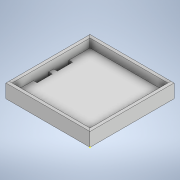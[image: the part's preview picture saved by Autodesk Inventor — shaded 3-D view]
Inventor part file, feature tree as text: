
AUTODESK INVENTOR PART (.ipt)
format: ipt  version: 2021 (Build 250183000, 183)  size: 198,656 bytes
history: native  units: in
note: dims shown in document units (in); Inventor stores cm internally (conversion verified against a paired STEP export)
features: sketch x5, extrude x4, projected_geometry x3, chamfer x2
ambient origin geometry x8: Origin, YZ Plane, XZ Plane, XY Plane, X Axis, Y Axis, Z Axis, Center Point
bodies: Solid1 (feature_tree)
feature tree (14):
  sketch  "Sketch1"  dims[d0=1.3071in d1=1.3071in]
  extrude  "Extrusion1"  Depth=1.3071in
  extrude  "Extrusion2"  Depth=0.0472in
  chamfer  "Chamfer1"  Distance=0.1575in
  extrude  "Extrusion3"  Depth=0.0787in TaperAngle=45.0deg
  extrude  "Extrusion4"  Depth=0.0394in
  chamfer  "Chamfer2"  Distance=0.0591in
  sketch  "Sketch2"  dims[d2=0.0787in d3=0.0in d4=0.0472in]
  sketch  "Sketch3"  dims[d5=0.0472in]
  projected_geometry  "Projected Loop1"
  sketch  "Sketch4"  dims[d6=1.2126in]
  projected_geometry  "Projected Loop2"
  sketch  "Sketch5"  dims[d7=1.2126in d8=0.1575in d9=0.0in d10=0.0236in d11=0.0787in d12=45.0deg d13=0.0394in d14=0.0591in d15=0.2362in d16=0.0394in d17=0.2362in d18=0.0394in d19=0.0591in d20=0.2362in d21=0.1575in d22=0.0in d25=0.2559in d26=1.1811in d27=0.5118in d28=0.0394in d29=0.0394in d30=0.4331in d31=1.1024in d32=0.0394in d33=0.0in d34=0.0197in d35=0.0787in d36=45.0deg]
  projected_geometry  "Projected Loop3"
